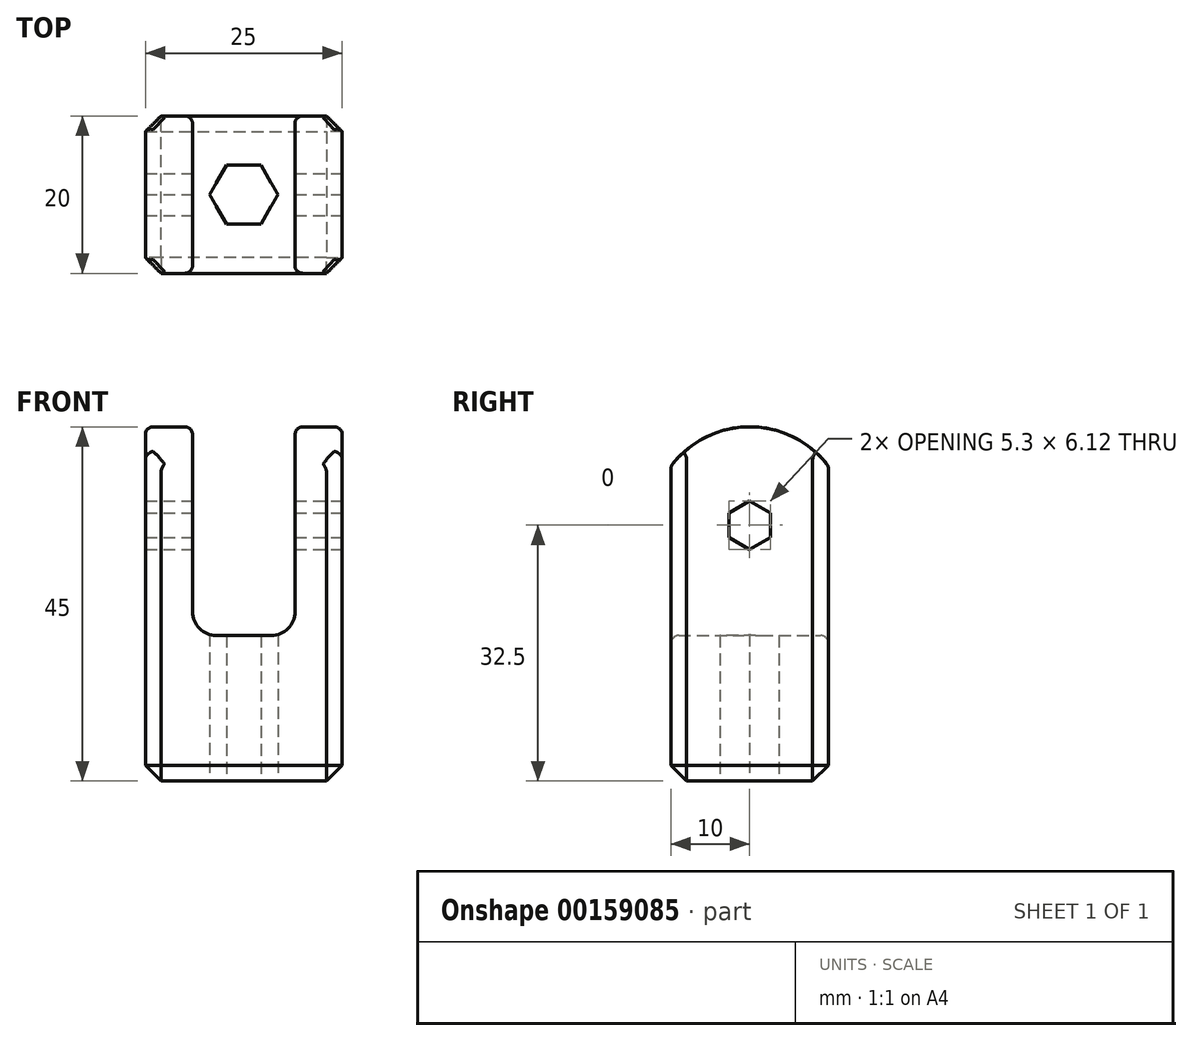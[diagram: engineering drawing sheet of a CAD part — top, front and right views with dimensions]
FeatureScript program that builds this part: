
annotation { "Feature Type Name" : "Feature", "Feature Type Description" : "" }
export const myFeature = defineFeature(function(context is Context, id is Id, definition is map)
    precondition{}
    {
        {
            var Q0;
            Q0=qCreatedBy(makeId("Top.planeOp"),FACE);
            var sketch = newSketch(context, id + "F0", { "sketchPlane" : qUnion([Q0])});
            skLineSegment(sketch, "E0.bottom", {"start": v(12.5, 10) * mm, "end": v(-12.5, 10) * mm});
            skLineSegment(sketch, "E0.top", {"start": v(12.5, -10) * mm, "end": v(-12.5, -10) * mm});
            skLineSegment(sketch, "E0.left", {"start": v(12.5, 10) * mm, "end": v(12.5, -10) * mm});
            skLineSegment(sketch, "E0.right", {"start": v(-12.5, 10) * mm, "end": v(-12.5, -10) * mm});
            skPoint(sketch, "E0.middle", {"position": v(0, 0) * mm});
            skPoint(sketch, "E1.visualSharp", {"position": v(-12.5, 10) * mm});
            skPoint(sketch, "E2.visualSharp", {"position": v(-12.5, -10) * mm});
            skPoint(sketch, "E3.visualSharp", {"position": v(12.5, -10) * mm});
            skPoint(sketch, "E4.visualSharp", {"position": v(12.5, 10) * mm});
            skSolve(sketch);
        }
        {
            var Q0;
            Q0 = qSketchRegion(id + "F0", true);
            extrude(context, id + "F1", {"entities" : qUnion([Q0]), "depth" : 45 * mm});
        }
        {
            var Q0;
            Q0=makeQuery(id+"F1.opExtrude","CAP_FACE",FACE,{"disambiguationData":[OSD([sQuery(id+"F0.wireOp",EDGE,"E0.bottom"),sQuery(id+"F0.wireOp",EDGE,"E0.top"),sQuery(id+"F0.wireOp",EDGE,"E0.left"),sQuery(id+"F0.wireOp",EDGE,"E0.right"),sQuery(id+"F0.wireOp",EDGE,"E1.filletArc"),sQuery(id+"F0.wireOp",EDGE,"E2.filletArc"),sQuery(id+"F0.wireOp",EDGE,"E3.filletArc"),sQuery(id+"F0.wireOp",EDGE,"E4.filletArc")])],"isStart":true});
            var sketch = newSketch(context, id + "F2", { "sketchPlane" : qUnion([Q0])});
            skPoint(sketch, "E5", {"position": v(0, 0) * mm});
            skCircle(sketch, "E6.cCircle", {"center": v(0, 0) * mm, "radius": 3.75 * mm, "construction": true});
            skLineSegment(sketch, "E6.0", {"start": v(2.17, 3.75) * mm, "end": v(4.33, 0) * mm});
            skLineSegment(sketch, "E6.1", {"start": v(4.33, 0) * mm, "end": v(2.17, -3.75) * mm});
            skLineSegment(sketch, "E6.2", {"start": v(2.17, -3.75) * mm, "end": v(-2.17, -3.75) * mm});
            skLineSegment(sketch, "E6.3", {"start": v(-2.17, -3.75) * mm, "end": v(-4.33, 0) * mm});
            skLineSegment(sketch, "E6.4", {"start": v(-4.33, 0) * mm, "end": v(-2.17, 3.75) * mm});
            skLineSegment(sketch, "E6.5", {"start": v(-2.17, 3.75) * mm, "end": v(2.17, 3.75) * mm});
            skPoint(sketch, "E6.0.midPoint", {"position": v(3.25, 1.88) * mm});
            skSolve(sketch);
        }
        {
            var Q0;
            Q0=qCreatedBy(makeId("Right.planeOp"),FACE);
            var sketch = newSketch(context, id + "F3", { "sketchPlane" : qUnion([Q0])});
            skLineSegment(sketch, "E7", {"start": v(-12.57, 32.5) * mm, "end": v(12.47, 32.5) * mm, "construction": true});
            skPoint(sketch, "E8", {"position": v(12.5, 32.5) * mm});
            skPoint(sketch, "E9", {"position": v(-12.5, 32.5) * mm});
            skArc(sketch, "E10", {"start": v(12.5, 32.5) * mm, "mid": v(0, 45) * mm, "end": v(-12.5, 32.5) * mm});
            skLineSegment(sketch, "E11", {"start": v(-12.5, 32.5) * mm, "end": v(-12.57, 32.5) * mm});
            skLineSegment(sketch, "E12", {"start": v(-12.57, 32.5) * mm, "end": v(-12.57, 47.78) * mm});
            skLineSegment(sketch, "E13", {"start": v(-12.57, 47.78) * mm, "end": v(12.47, 47.78) * mm});
            skLineSegment(sketch, "E14", {"start": v(12.47, 47.78) * mm, "end": v(12.47, 32.5) * mm});
            skLineSegment(sketch, "E15", {"start": v(12.47, 32.5) * mm, "end": v(12.5, 32.5) * mm});
            skLineSegment(sketch, "E16", {"start": v(-12.5, 5) * mm, "end": v(-12.5, 45) * mm, "construction": true});
            skLineSegment(sketch, "E17", {"start": v(12.5, 40) * mm, "end": v(12.5, 0) * mm, "construction": true});
            skSolve(sketch);
        }
        {
            var Q0;
            Q0=qCreatedBy(makeId("Right.planeOp"),FACE);
            var sketch = newSketch(context, id + "F4", { "sketchPlane" : qUnion([Q0])});
            skLineSegment(sketch, "E18.bottom", {"start": v(-14.84, 45) * mm, "end": v(15.16, 45) * mm});
            skLineSegment(sketch, "E18.top", {"start": v(-14.84, 18.5) * mm, "end": v(15.16, 18.5) * mm});
            skLineSegment(sketch, "E18.left", {"start": v(-14.84, 45) * mm, "end": v(-14.84, 18.5) * mm});
            skLineSegment(sketch, "E18.right", {"start": v(15.16, 45) * mm, "end": v(15.16, 18.5) * mm});
            skPoint(sketch, "E19", {"position": v(0, 32.5) * mm});
            skSolve(sketch);
        }
        {
            var Q0;
            Q0=qCreatedBy(makeId("Right.planeOp"),FACE);
            var sketch = newSketch(context, id + "F5", { "sketchPlane" : qUnion([Q0])});
            skCircle(sketch, "E20.cCircle", {"center": v(0, 32.5) * mm, "radius": 2.65 * mm, "construction": true});
            skLineSegment(sketch, "E20.0", {"start": v(0, 29.44) * mm, "end": v(-2.65, 30.97) * mm});
            skLineSegment(sketch, "E20.1", {"start": v(-2.65, 30.97) * mm, "end": v(-2.65, 34.03) * mm});
            skLineSegment(sketch, "E20.2", {"start": v(-2.65, 34.03) * mm, "end": v(0, 35.56) * mm});
            skLineSegment(sketch, "E20.3", {"start": v(0, 35.56) * mm, "end": v(2.65, 34.03) * mm});
            skLineSegment(sketch, "E20.4", {"start": v(2.65, 34.03) * mm, "end": v(2.65, 30.97) * mm});
            skLineSegment(sketch, "E20.5", {"start": v(2.65, 30.97) * mm, "end": v(0, 29.44) * mm});
            skPoint(sketch, "E20.0.midPoint", {"position": v(-1.32, 30.2) * mm});
            skSolve(sketch);
        }
        {
            var Q0;
            Q0 = qSketchRegion(id + "F3", true);
            extrude(context, id + "F6", {"entities" : qUnion([Q0]), "operationType" : NewBodyOperationType.REMOVE, "endBound" : BoundingType.THROUGH_ALL, "oppositeDirection" : true, "depth" : 25 * mm, "hasSecondDirection" : true, "secondDirectionBound" : BoundingType.THROUGH_ALL, "secondDirectionOppositeDirection" : false, "secondDirectionDepth" : 25 * mm});
        }
        {
            var Q0;
            Q0 = qSketchRegion(id + "F4", true);
            extrude(context, id + "F7", {"entities" : qUnion([Q0]), "operationType" : NewBodyOperationType.REMOVE, "depth" : 6.5 * mm, "hasSecondDirection" : true, "secondDirectionOppositeDirection" : true, "secondDirectionDepth" : 6.5 * mm});
        }
        {
            var Q0;
            Q0=makeQuery(id+"F7.boolean.opBoolean","COPY",EDGE,{"derivedFrom":makeQuery(id+"F7.opExtrude","CAP_EDGE",EDGE,{"disambiguationData":[OSD([sQuery(id+"F4.wireOp",EDGE,"E18.top")])],"isStart":false})});
            var Q1;
            Q1=makeQuery(id+"F7.boolean.opBoolean","COPY",EDGE,{"derivedFrom":makeQuery(id+"F7.opExtrude","CAP_EDGE",EDGE,{"disambiguationData":[OSD([sQuery(id+"F4.wireOp",EDGE,"E18.top")])],"isStart":true})});
            fillet(context, id + "F8", {"entities" : qUnion([Q0, Q1]), "radius" : 3 * mm, "tangentPropagation" : true, "allowEdgeOverflow" : false});
        }
        {
            var Q0;
            Q0=makeQuery(id+"F1.opExtrude","CAP_FACE",FACE,{"disambiguationData":[OSD([sQuery(id+"F0.wireOp",EDGE,"E0.bottom"),sQuery(id+"F0.wireOp",EDGE,"E0.top"),sQuery(id+"F0.wireOp",EDGE,"E0.left"),sQuery(id+"F0.wireOp",EDGE,"E0.right"),sQuery(id+"F0.wireOp",EDGE,"E1.filletArc"),sQuery(id+"F0.wireOp",EDGE,"E2.filletArc"),sQuery(id+"F0.wireOp",EDGE,"E3.filletArc"),sQuery(id+"F0.wireOp",EDGE,"E4.filletArc")])],"isStart":true});
            var Q1;
            Q1=makeQuery(id+"F1.opExtrude","SWEPT_EDGE",EDGE,{"disambiguationData":[OSD([sQuery(id+"F0.wireOp",EDGE,"E0.bottom"),sQuery(id+"F0.wireOp",EDGE,"E0.right")])]});
            var Q2;
            Q2=makeQuery(id+"F1.opExtrude","SWEPT_EDGE",EDGE,{"disambiguationData":[OSD([sQuery(id+"F0.wireOp",EDGE,"E0.bottom"),sQuery(id+"F0.wireOp",EDGE,"E0.left")])]});
            var Q3;
            Q3=makeQuery(id+"F1.opExtrude","SWEPT_EDGE",EDGE,{"disambiguationData":[OSD([sQuery(id+"F0.wireOp",EDGE,"E0.top"),sQuery(id+"F0.wireOp",EDGE,"E0.right")])]});
            var Q4;
            Q4=makeQuery(id+"F1.opExtrude","SWEPT_EDGE",EDGE,{"disambiguationData":[OSD([sQuery(id+"F0.wireOp",EDGE,"E0.top"),sQuery(id+"F0.wireOp",EDGE,"E0.left")])]});
            chamfer(context, id + "F9", {"entities" : qUnion([Q0, Q1, Q2, Q3, Q4]), "width" : 2 * mm, "tangentPropagation" : true});
        }
        {
            var Q0;
            Q0=makeQuery(id+"F7.boolean.opBoolean","COPY",FACE,{"derivedFrom":makeQuery(id+"F7.opExtrude","CAP_FACE",FACE,{"disambiguationData":[OSD([sQuery(id+"F4.wireOp",EDGE,"E18.bottom"),sQuery(id+"F4.wireOp",EDGE,"E18.top"),sQuery(id+"F4.wireOp",EDGE,"E18.left"),sQuery(id+"F4.wireOp",EDGE,"E18.right")])],"isStart":false})});
            var Q1;
            {var subQ0=sQuery(id+"F3.wireOp",EDGE,"E10");Q1=makeQuery(id+"F7.boolean.opBoolean","SPLIT",FACE,{"disambiguationData":[TD([makeQuery(id+"F1.opExtrude","SWEPT_FACE",FACE,{"disambiguationData":[OSD([sQuery(id+"F0.wireOp",EDGE,"E0.right")])]})])],"derivedFrom":makeQuery(id+"F6.boolean.opBoolean","COPY",FACE,{"derivedFrom":makeQuery(id+"F6.opExtrude","SWEPT_FACE",FACE,{"disambiguationData":[OSD([subQ0]),TDD([makeQuery(id+"F3.imprint","IMPRINT",EDGE,{"disambiguationData":[TD([[makeQuery(id+"F3.imprint","INTERSECT",VERTEX,{"derivedFrom":[subQ0,sQuery(id+"F3.wireOp",EDGE,"E11")]}),1.0]])],"derivedFrom":subQ0})])]})})});}
            var Q2;
            {var subQ0=sQuery(id+"F3.wireOp",EDGE,"E10");Q2=makeQuery(id+"F7.boolean.opBoolean","SPLIT",FACE,{"disambiguationData":[TD([makeQuery(id+"F1.opExtrude","SWEPT_FACE",FACE,{"disambiguationData":[OSD([sQuery(id+"F0.wireOp",EDGE,"E0.left")])]})])],"derivedFrom":makeQuery(id+"F6.boolean.opBoolean","COPY",FACE,{"derivedFrom":makeQuery(id+"F6.opExtrude","SWEPT_FACE",FACE,{"disambiguationData":[OSD([subQ0]),TDD([makeQuery(id+"F3.imprint","IMPRINT",EDGE,{"disambiguationData":[TD([[makeQuery(id+"F3.imprint","INTERSECT",VERTEX,{"derivedFrom":[subQ0,sQuery(id+"F3.wireOp",EDGE,"E11")]}),1.0]])],"derivedFrom":subQ0})])]})})});}
            fillet(context, id + "F10", {"entities" : qUnion([Q0, Q1, Q2]), "radius" : 1 * mm, "tangentPropagation" : true, "allowEdgeOverflow" : false});
        }
        {
            var Q0;
            Q0 = qSketchRegion(id + "F5", true);
            extrude(context, id + "F11", {"entities" : qUnion([Q0]), "operationType" : NewBodyOperationType.REMOVE, "endBound" : BoundingType.THROUGH_ALL, "oppositeDirection" : true, "depth" : 25 * mm, "hasSecondDirection" : true, "secondDirectionBound" : BoundingType.THROUGH_ALL, "secondDirectionOppositeDirection" : false, "secondDirectionDepth" : 25 * mm});
        }
        {
            var Q0;
            Q0 = qSketchRegion(id + "F2", true);
            extrude(context, id + "F12", {"entities" : qUnion([Q0]), "operationType" : NewBodyOperationType.REMOVE, "oppositeDirection" : true, "depth" : 25 * mm});
        }
    });
